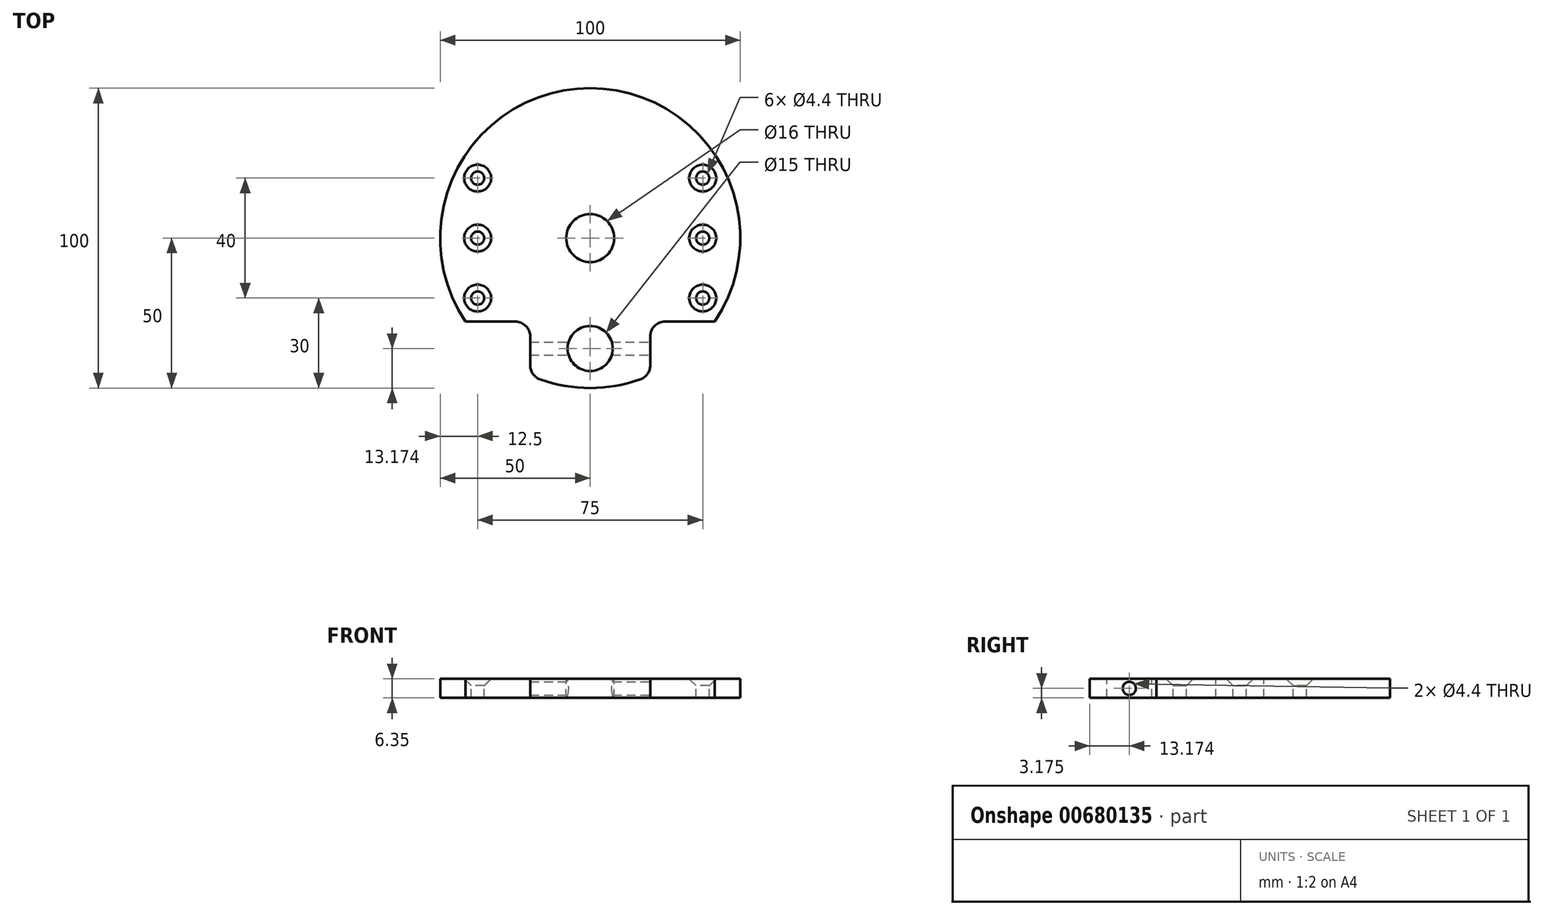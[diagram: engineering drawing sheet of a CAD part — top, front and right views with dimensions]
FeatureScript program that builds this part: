
annotation { "Feature Type Name" : "Feature", "Feature Type Description" : "" }
export const myFeature = defineFeature(function(context is Context, id is Id, definition is map)
    precondition{}
    {
        {
            var Q0;
            Q0=qCreatedBy(makeId("Top.planeOp"),FACE);
            var sketch = newSketch(context, id + "F0", { "sketchPlane" : qUnion([Q0])});
            skCircle(sketch, "E0", {"center": v(0, 0) * mm, "radius": 50 * mm});
            skSolve(sketch);
        }
        {
            var Q0;
            Q0=makeQuery(id+"F0.imprint","IMPRINT",FACE,{"disambiguationData":[TD([[makeQuery(id+"F0.imprint","IMPRINT",EDGE,{"derivedFrom":sQuery(id+"F0.wireOp",EDGE,"E0")}),1.0]])]});
            extrude(context, id + "F1", {"entities" : qUnion([Q0]), "depth" : 6.35 * mm, "offsetDistance" : 25 * mm});
        }
        {
            var Q0;
            Q0=makeQuery(id+"F1.opExtrude","CAP_FACE",FACE,{"disambiguationData":[OSD([sQuery(id+"F0.wireOp",EDGE,"E0")])],"isStart":false});
            var sketch = newSketch(context, id + "F2", { "sketchPlane" : qUnion([Q0])});
            skPoint(sketch, "E1", {"position": v(-37.5, 20) * mm});
            skPoint(sketch, "E2", {"position": v(-37.5, 0) * mm});
            skPoint(sketch, "E3", {"position": v(-37.5, -20) * mm});
            skPoint(sketch, "E4", {"position": v(37.5, -20) * mm});
            skPoint(sketch, "E5", {"position": v(37.5, 0) * mm});
            skPoint(sketch, "E6", {"position": v(37.5, 20) * mm});
            skLineSegment(sketch, "E7", {"start": v(-37.5, 20) * mm, "end": v(-37.5, 0) * mm, "construction": true});
            skLineSegment(sketch, "E8", {"start": v(-37.5, 0) * mm, "end": v(-37.5, -20) * mm, "construction": true});
            skLineSegment(sketch, "E9", {"start": v(37.5, -20) * mm, "end": v(37.5, 0) * mm, "construction": true});
            skLineSegment(sketch, "E10", {"start": v(37.5, 0) * mm, "end": v(37.5, 20) * mm, "construction": true});
            skLineSegment(sketch, "E11", {"start": v(-37.5, 20) * mm, "end": v(37.5, 20) * mm, "construction": true});
            skLineSegment(sketch, "E12", {"start": v(37.5, -20) * mm, "end": v(-37.5, -20) * mm, "construction": true});
            skLineSegment(sketch, "E13", {"start": v(0, 20) * mm, "end": v(0, -20) * mm, "construction": true});
            skSolve(sketch);
        }
        {
            var Q0;
            Q0=sQuery(id+"F2.wireOp",VERTEX,"E1");
            var Q1;
            Q1=sQuery(id+"F2.wireOp",VERTEX,"E2");
            var Q2;
            Q2=sQuery(id+"F2.wireOp",VERTEX,"E3");
            var Q3;
            Q3=sQuery(id+"F2.wireOp",VERTEX,"E6");
            var Q4;
            Q4=sQuery(id+"F2.wireOp",VERTEX,"E5");
            var Q5;
            Q5=sQuery(id+"F2.wireOp",VERTEX,"E4");
            var Q6;
            Q6=makeQuery(id+"F1.opExtrude","SWEPT_BODY",BODY,{"disambiguationData":[OSD([sQuery(id+"F0.wireOp",EDGE,"E0")])]});
            hole(context, id + "F3", {"style" : HoleStyle.C_SINK, "endStyle" : HoleEndStyle.THROUGH, "standardTappedOrClearance" : lookupTablePath({ "standard" : "ISO", "fit" : "Normal", "size" : "M4", "type" : "Clearance" }), "standardBlindInLast" : lookupTablePath({ "fit" : "Standard", "standard" : "ISO", "size" : "M4", "type" : "Clearance" }), "holeDiameter" : 4.4 * mm, "cSinkDiameter" : 8.96 * mm, "cSinkAngle" : 90 * degree, "majorDiameter" : 5 * mm, "isTappedThrough" : true, "tappedDepth" : 12 * mm, "tapClearance" : 3, "locations" : qUnion([Q0, Q1, Q2, Q3, Q4, Q5]), "scope" : qUnion([Q6])});
        }
        {
            var Q0;
            Q0=makeQuery(id+"F1.opExtrude","CAP_FACE",FACE,{"disambiguationData":[OSD([sQuery(id+"F0.wireOp",EDGE,"E0")])],"isStart":false});
            var sketch = newSketch(context, id + "F4", { "sketchPlane" : qUnion([Q0])});
            skCircle(sketch, "E14", {"center": v(0, 0) * mm, "radius": 8 * mm});
            skSolve(sketch);
        }
        {
            var Q0;
            Q0=makeQuery(id+"F4.imprint","IMPRINT",FACE,{"disambiguationData":[TD([[makeQuery(id+"F4.imprint","IMPRINT",EDGE,{"derivedFrom":sQuery(id+"F4.wireOp",EDGE,"E14")}),1.0]])]});
            extrude(context, id + "F5", {"entities" : qUnion([Q0]), "operationType" : NewBodyOperationType.REMOVE, "oppositeDirection" : true, "depth" : 8 * mm, "offsetDistance" : 25 * mm});
        }
        {
            var Q0;
            Q0=makeQuery(id+"F1.opExtrude","CAP_FACE",FACE,{"disambiguationData":[OSD([sQuery(id+"F0.wireOp",EDGE,"E0")])],"isStart":false});
            var sketch = newSketch(context, id + "F6", { "sketchPlane" : qUnion([Q0])});
            skLineSegment(sketch, "E15", {"start": v(-41.54, -27.83) * mm, "end": v(-20, -27.83) * mm});
            skLineSegment(sketch, "E16", {"start": v(-20, -27.83) * mm, "end": v(-20, -45.83) * mm});
            skLineSegment(sketch, "E17", {"start": v(41.54, -27.83) * mm, "end": v(20, -27.83) * mm});
            skLineSegment(sketch, "E18", {"start": v(20, -27.83) * mm, "end": v(20, -45.83) * mm});
            skLineSegment(sketch, "E19", {"start": v(-20, -27.83) * mm, "end": v(20, -27.83) * mm, "construction": true});
            skArc(sketch, "E20", {"start": v(-41.54, -27.83) * mm, "mid": v(-32.06, -38.37) * mm, "end": v(-20, -45.83) * mm});
            skArc(sketch, "E21", {"start": v(41.54, -27.83) * mm, "mid": v(32.06, -38.37) * mm, "end": v(20, -45.83) * mm});
            skSolve(sketch);
        }
        {
            var Q0;
            Q0 = qSketchRegion(id + "F6", true);
            extrude(context, id + "F7", {"entities" : qUnion([Q0]), "operationType" : NewBodyOperationType.REMOVE, "oppositeDirection" : true, "depth" : 25 * mm, "offsetDistance" : 25 * mm});
        }
        {
            var Q0;
            Q0=makeQuery(id+"F7.boolean.opBoolean","COPY",FACE,{"derivedFrom":makeQuery(id+"F7.opExtrude","SWEPT_FACE",FACE,{"disambiguationData":[OSD([sQuery(id+"F6.wireOp",EDGE,"E18")])]})});
            var sketch = newSketch(context, id + "F8", { "sketchPlane" : qUnion([Q0])});
            skPoint(sketch, "E22", {"position": v(-36.83, 3.18) * mm});
            skPoint(sketch, "E22.positionSnap0", {"position": v(-36.83, 0) * mm});
            skLineSegment(sketch, "E23", {"start": v(-36.83, 6.35) * mm, "end": v(-36.83, 0) * mm, "construction": true});
            skSolve(sketch);
        }
        {
            var Q0;
            Q0=makeQuery(id+"F7.boolean.opBoolean","COPY",EDGE,{"derivedFrom":makeQuery(id+"F7.opExtrude","SWEPT_EDGE",EDGE,{"disambiguationData":[OSD([sQuery(id+"F0.wireOp",EDGE,"E0"),sQuery(id+"F6.wireOp",EDGE,"E15"),sQuery(id+"F6.wireOp",EDGE,"E20")])]})});
            var Q1;
            Q1=makeQuery(id+"F7.boolean.opBoolean","COPY",EDGE,{"derivedFrom":makeQuery(id+"F7.opExtrude","SWEPT_EDGE",EDGE,{"disambiguationData":[OSD([sQuery(id+"F0.wireOp",EDGE,"E0"),sQuery(id+"F6.wireOp",EDGE,"E16"),sQuery(id+"F6.wireOp",EDGE,"E20")])]})});
            var Q2;
            Q2=makeQuery(id+"F7.boolean.opBoolean","COPY",EDGE,{"derivedFrom":makeQuery(id+"F7.opExtrude","SWEPT_EDGE",EDGE,{"disambiguationData":[OSD([sQuery(id+"F6.wireOp",EDGE,"E15"),sQuery(id+"F6.wireOp",EDGE,"E16")])]})});
            var Q3;
            Q3=makeQuery(id+"F7.boolean.opBoolean","COPY",EDGE,{"derivedFrom":makeQuery(id+"F7.opExtrude","SWEPT_EDGE",EDGE,{"disambiguationData":[OSD([sQuery(id+"F6.wireOp",EDGE,"E17"),sQuery(id+"F6.wireOp",EDGE,"E18")])]})});
            var Q4;
            Q4=makeQuery(id+"F7.boolean.opBoolean","COPY",EDGE,{"derivedFrom":makeQuery(id+"F7.opExtrude","SWEPT_EDGE",EDGE,{"disambiguationData":[OSD([sQuery(id+"F0.wireOp",EDGE,"E0"),sQuery(id+"F6.wireOp",EDGE,"E18"),sQuery(id+"F6.wireOp",EDGE,"E21")])]})});
            var Q5;
            Q5=makeQuery(id+"F7.boolean.opBoolean","COPY",EDGE,{"derivedFrom":makeQuery(id+"F7.opExtrude","SWEPT_EDGE",EDGE,{"disambiguationData":[OSD([sQuery(id+"F0.wireOp",EDGE,"E0"),sQuery(id+"F6.wireOp",EDGE,"E17"),sQuery(id+"F6.wireOp",EDGE,"E21")])]})});
            fillet(context, id + "F9", {"entities" : qUnion([Q0, Q1, Q2, Q3, Q4, Q5]), "radius" : 5 * mm, "tangentPropagation" : true, "allowEdgeOverflow" : false});
        }
        {
            var Q0;
            Q0=sQuery(id+"F8.wireOp",VERTEX,"E22");
            var Q1;
            Q1=makeQuery(id+"F1.opExtrude","SWEPT_BODY",BODY,{"disambiguationData":[OSD([sQuery(id+"F0.wireOp",EDGE,"E0")])]});
            hole(context, id + "F10", {"style" : HoleStyle.SIMPLE, "endStyle" : HoleEndStyle.THROUGH, "standardTappedOrClearance" : lookupTablePath({ "standard" : "ISO", "fit" : "Normal", "size" : "M4", "type" : "Clearance" }), "standardBlindInLast" : lookupTablePath({ "fit" : "Standard", "standard" : "ISO", "size" : "M4", "type" : "Clearance" }), "holeDiameter" : 4.4 * mm, "majorDiameter" : 5 * mm, "isTappedThrough" : true, "tappedDepth" : 12 * mm, "tapClearance" : 3, "locations" : qUnion([Q0]), "scope" : qUnion([Q1])});
        }
        {
            var Q0;
            Q0=makeQuery(id+"F1.opExtrude","CAP_FACE",FACE,{"disambiguationData":[OSD([sQuery(id+"F0.wireOp",EDGE,"E0")])],"isStart":false});
            var sketch = newSketch(context, id + "F11", { "sketchPlane" : qUnion([Q0])});
            skLineSegment(sketch, "E24", {"start": v(7.5, -36.83) * mm, "end": v(20, -36.83) * mm, "construction": true});
            skLineSegment(sketch, "E25", {"start": v(-7.5, -36.83) * mm, "end": v(-20, -36.83) * mm, "construction": true});
            skCircle(sketch, "E26", {"center": v(0, -36.83) * mm, "radius": 7.5 * mm});
            skSolve(sketch);
        }
        {
            var Q0;
            Q0=makeQuery(id+"F11.imprint","IMPRINT",FACE,{"disambiguationData":[TD([[makeQuery(id+"F11.imprint","IMPRINT",EDGE,{"derivedFrom":sQuery(id+"F11.wireOp",EDGE,"mkUnKuM3-oAfV-fDU4-qRTJ-F4UNty4UeYOD.bottom")}),-1.0]])]});
            var Q1;
            Q1=makeQuery(id+"F11.imprint","IMPRINT",FACE,{"disambiguationData":[TD([[makeQuery(id+"F11.imprint","IMPRINT",EDGE,{"derivedFrom":sQuery(id+"F11.wireOp",EDGE,"E26")}),1.0]])]});
            extrude(context, id + "F12", {"entities" : qUnion([Q0, Q1]), "operationType" : NewBodyOperationType.REMOVE, "oppositeDirection" : true, "depth" : 25 * mm, "offsetDistance" : 25 * mm});
        }
    });
